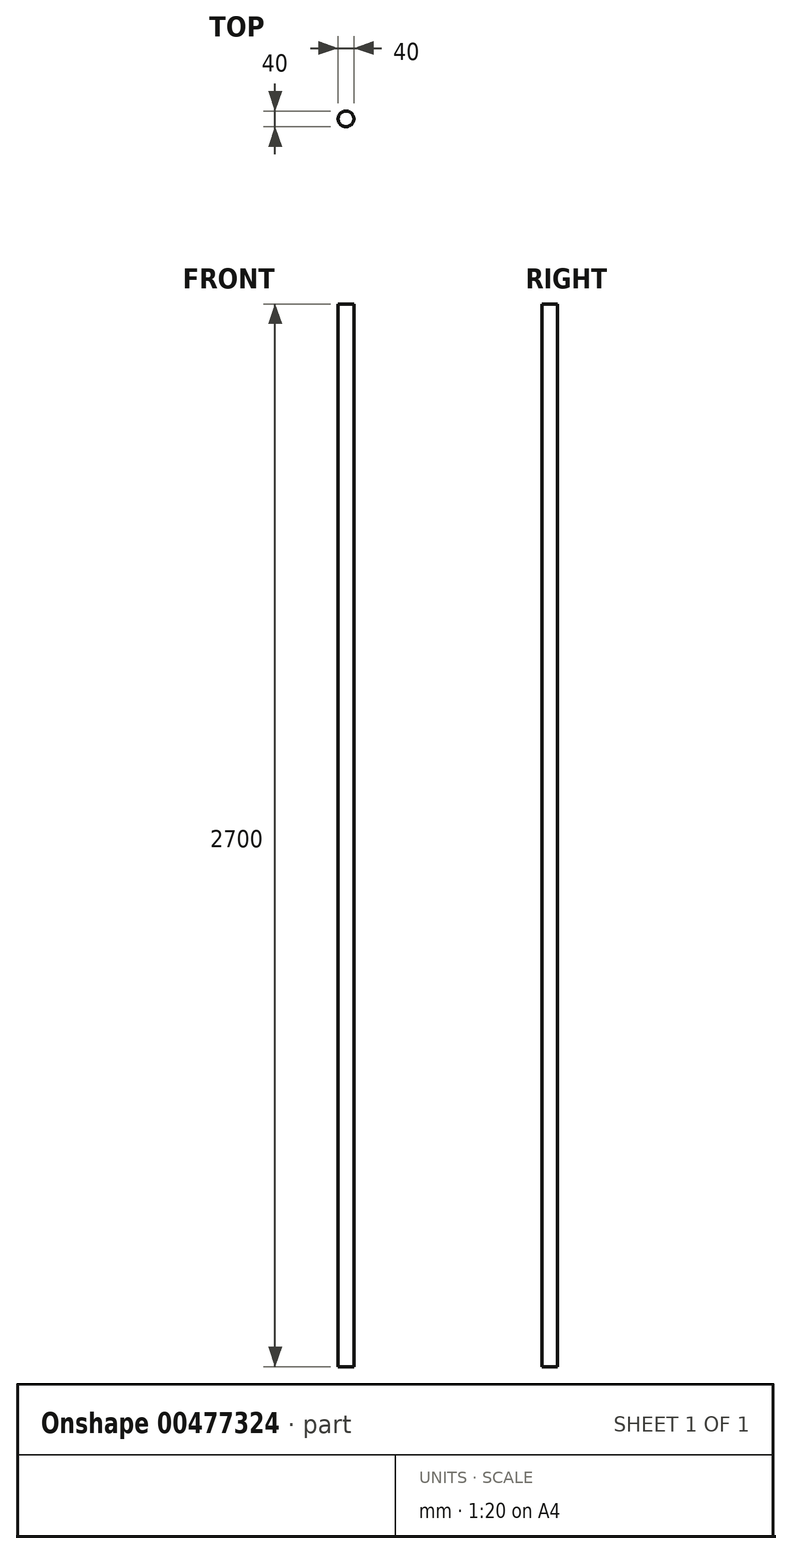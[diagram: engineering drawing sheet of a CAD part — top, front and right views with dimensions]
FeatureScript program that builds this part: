
annotation { "Feature Type Name" : "Feature", "Feature Type Description" : "" }
export const myFeature = defineFeature(function(context is Context, id is Id, definition is map)
    precondition{}
    {
        {
            var Q0;
            Q0=qCreatedBy(makeId("Top.planeOp"),FACE);
            var sketch = newSketch(context, id + "F0", { "sketchPlane" : qUnion([Q0])});
            skCircle(sketch, "E0", {"center": v(0, 0) * mm, "radius": 20 * mm});
            skSolve(sketch);
        }
        {
            var Q0;
            Q0 = qSketchRegion(id + "F0", true);
            extrude(context, id + "F1", {"entities" : qUnion([Q0]), "depth" : 2700 * mm});
        }
    });
